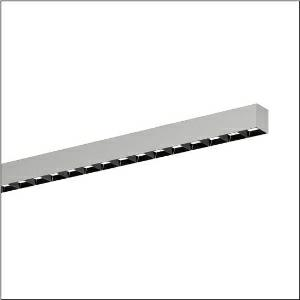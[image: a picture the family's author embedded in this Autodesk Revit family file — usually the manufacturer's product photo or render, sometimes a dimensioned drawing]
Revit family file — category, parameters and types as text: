
# Revit family: silica_r__21_51mx22tctas_2eab
name_source: partatom
category: Lighting Fixtures
units: mm (PartAtom-declared; Revit-internal decimal feet)

## family parameters
Cut with Voids When Loaded = No
Host = Face
Light Source = No
Part Type = Normal
Room Calculation Point = No
Round Connector Dimension = Use Diameter
Shared = No

## types (1)
- --- (1 x LED, 9300 lm, 80.4 W, 6500K)
    Apparent Load = 80 VA
    CIE Flux Codes = 84 100 100 100 100
    Color Rendering = 80
    Color Temperature = 6500K
    Default Elevation = 1800 mm
    Description = Silica® 21, office luminaire, primary light control with darklight reflector, of PMMA, black, CAT 2 (L<= 3000cd/m²), light emission: direct distribution, primary light characteristic: symmetric, installation type: surface-mounted, LED, rated luminous flux: 9.300lm, luminous efficacy: 110lm/W, light colour: 8tw, colour temperature: 2700..6500K, control gear: DALI DT8, with terminal, 3+2-pole, max. 2.5mm², mains connection: 220..240V, AC, 50/60Hz, rated input power: 84.5W, luminaire housing, of aluminium, metallic grey (RAL 9006), length: 3.004mm, width: 53mm, height: 53mm, protection rating (complete): IP20, insulation class (complete): insulation class I (protective earthing), certification: CE, permissible operating ambient temperature: 0..+35°C, standard: EN 50419, packaging unit: 1 piece
    Height = 53 mm
    Lamp = 1 x LED
    Lamp Light Flux = 9300 lm
    Lamp Power = 80.4 W
    Lamp count = 1
    Length = 3004 mm
    Luminous efficacy = 116 lm/W
    Manufacturer = Siteco
    ModVariant = No
    Model = 51MX22TCTAS
    Mounting Place = Ceiling
    Mounting Type = Surface mounted
    Number of Poles = 1
    OnlyDefault = Yes
    Power Factor = 1
    Product Name = Silica® 21
    Product group = office luminaire | ceiling mounted
    ProductGroupID = 302
    Protection Class = Protection class I
    Protection Degree = IP 20
    RLX_Detail_Level = 1
    RLX_Emergency_Light_Flux = 0 lm
    RLX_Emergency_Type = 0
    RLX_Emergency_Type_DB = No
    RlxData = <blob elided: 59997 chars, md5=2ad36491>
    Socket = socket
    Standby Power = 0 W
    System Light Flux = 9300 lm
    System Power = 80 W
    Type Comments = individual setting
    Type Image = l_1335929.jpg
    URL = http://relux.com
    VarID = @adj_140112
    Voltage = 0 V
    Weight = 0.00 kg
    Width = 53 mm

## geometry (parser evidence)
native form markers: Blend x4, Sweep x11
no freeform markers — native parametric forms only
